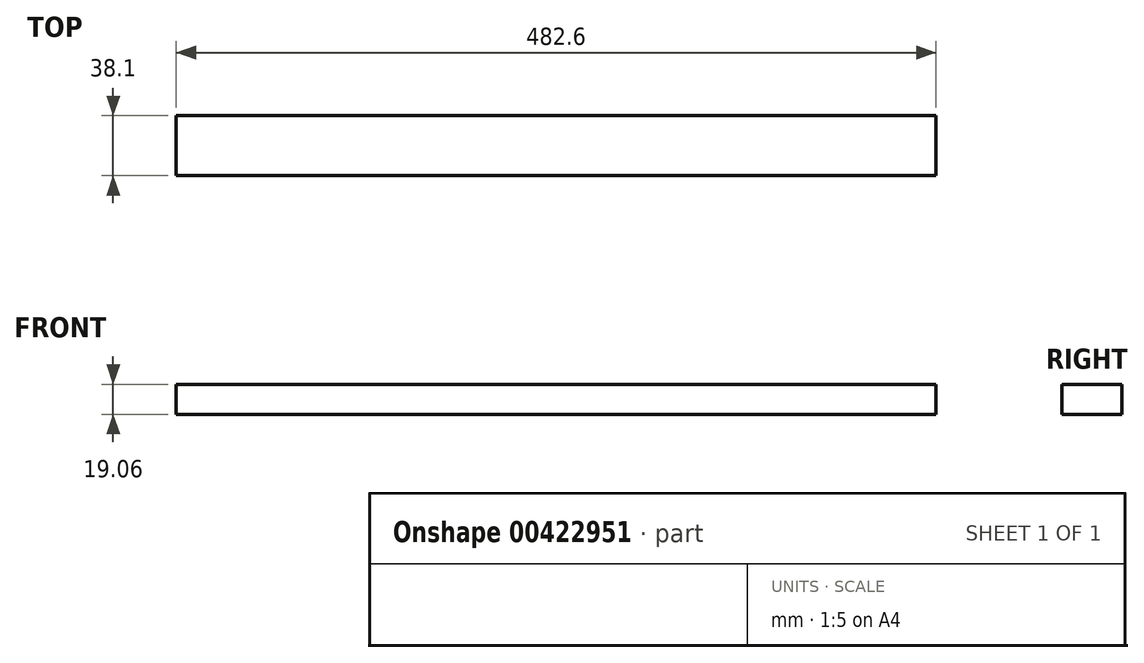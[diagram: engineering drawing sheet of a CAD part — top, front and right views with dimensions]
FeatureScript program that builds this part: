
annotation { "Feature Type Name" : "Feature", "Feature Type Description" : "" }
export const myFeature = defineFeature(function(context is Context, id is Id, definition is map)
    precondition{}
    {
        {
            var Q0;
            Q0=qCreatedBy(makeId("Front.planeOp"),FACE);
            var sketch = newSketch(context, id + "F0", { "sketchPlane" : qUnion([Q0])});
            skLineSegment(sketch, "E0.bottom", {"start": v(241.3, 9.52) * mm, "end": v(-241.3, 9.52) * mm});
            skLineSegment(sketch, "E0.top", {"start": v(241.3, -9.52) * mm, "end": v(-241.3, -9.52) * mm});
            skLineSegment(sketch, "E0.left", {"start": v(241.3, 9.52) * mm, "end": v(241.3, -9.52) * mm});
            skLineSegment(sketch, "E0.right", {"start": v(-241.3, 9.52) * mm, "end": v(-241.3, -9.52) * mm});
            skPoint(sketch, "E0.middle", {"position": v(0, 0) * mm});
            skSolve(sketch);
        }
        {
            var Q0;
            Q0 = qSketchRegion(id + "F0", true);
            extrude(context, id + "F1", {"entities" : qUnion([Q0]), "depth" : 38.1 * mm, "offsetDistance" : 25.4 * mm});
        }
    });
